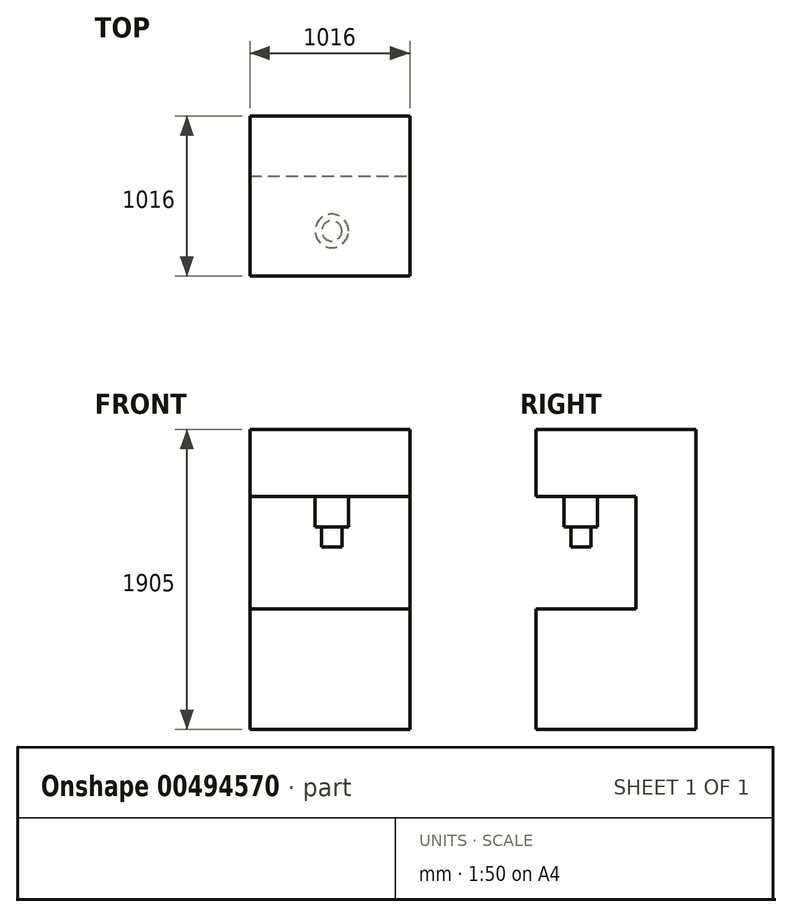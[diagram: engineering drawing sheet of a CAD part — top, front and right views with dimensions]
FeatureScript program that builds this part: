
annotation { "Feature Type Name" : "Feature", "Feature Type Description" : "" }
export const myFeature = defineFeature(function(context is Context, id is Id, definition is map)
    precondition{}
    {
        {
            var Q0;
            Q0=qCreatedBy(makeId("Front.planeOp"),FACE);
            var sketch = newSketch(context, id + "F0", { "sketchPlane" : qUnion([Q0])});
            skLineSegment(sketch, "E0.bottom", {"start": v(0, 0) * mm, "end": v(-1016, 0) * mm});
            skLineSegment(sketch, "E0.top", {"start": v(0, 1905) * mm, "end": v(-1016, 1905) * mm});
            skLineSegment(sketch, "E0.left", {"start": v(0, 0) * mm, "end": v(0, 1905) * mm});
            skLineSegment(sketch, "E0.right", {"start": v(-1016, 0) * mm, "end": v(-1016, 1905) * mm});
            skSolve(sketch);
        }
        {
            var Q0;
            Q0=makeQuery(id+"F0.imprint","IMPRINT",FACE,{"disambiguationData":[TD([[makeQuery(id+"F0.imprint","IMPRINT",EDGE,{"derivedFrom":sQuery(id+"F0.wireOp",EDGE,"E0.bottom")}),-1.0]])]});
            extrude(context, id + "F1", {"entities" : qUnion([Q0]), "depth" : 1016 * mm});
        }
        {
            var Q0;
            Q0=makeQuery(id+"F1.opExtrude","CAP_FACE",FACE,{"disambiguationData":[OSD([sQuery(id+"F0.wireOp",EDGE,"E0.bottom"),sQuery(id+"F0.wireOp",EDGE,"E0.top"),sQuery(id+"F0.wireOp",EDGE,"E0.left"),sQuery(id+"F0.wireOp",EDGE,"E0.right")])],"isStart":false});
            var sketch = newSketch(context, id + "F2", { "sketchPlane" : qUnion([Q0])});
            skLineSegment(sketch, "E1.bottom", {"start": v(-1016, 1478.3) * mm, "end": v(0, 1478.3) * mm});
            skLineSegment(sketch, "E1.top", {"start": v(-1016, 765.22) * mm, "end": v(0, 765.22) * mm});
            skLineSegment(sketch, "E1.left", {"start": v(-1016, 1478.3) * mm, "end": v(-1016, 765.22) * mm});
            skLineSegment(sketch, "E1.right", {"start": v(0, 1478.3) * mm, "end": v(0, 765.22) * mm});
            skSolve(sketch);
        }
        {
            var Q0;
            Q0=makeQuery(id+"F2.imprint","IMPRINT",FACE,{"disambiguationData":[TD([[makeQuery(id+"F2.imprint","IMPRINT",EDGE,{"derivedFrom":sQuery(id+"F2.wireOp",EDGE,"E1.bottom")}),-1.0]])]});
            extrude(context, id + "F3", {"entities" : qUnion([Q0]), "operationType" : NewBodyOperationType.REMOVE, "oppositeDirection" : true, "depth" : 635 * mm});
        }
        {
            var Q0;
            Q0=makeQuery(id+"F3.boolean.opBoolean","COPY",FACE,{"derivedFrom":makeQuery(id+"F3.opExtrude","SWEPT_FACE",FACE,{"disambiguationData":[OSD([sQuery(id+"F2.wireOp",EDGE,"E1.bottom")])]})});
            var sketch = newSketch(context, id + "F4", { "sketchPlane" : qUnion([Q0])});
            skCircle(sketch, "E2", {"center": v(-495.64, 729.41) * mm, "radius": 106.51 * mm});
            skSolve(sketch);
        }
        {
            var Q0;
            Q0 = qSketchRegion(id + "F4", true);
            extrude(context, id + "F5", {"entities" : qUnion([Q0]), "operationType" : NewBodyOperationType.ADD, "depth" : 193.04 * mm});
        }
        {
            var Q0;
            Q0=makeQuery(id+"F5.opExtrude","CAP_FACE",FACE,{"disambiguationData":[OSD([sQuery(id+"F4.wireOp",EDGE,"E2")])],"isStart":false});
            var sketch = newSketch(context, id + "F6", { "sketchPlane" : qUnion([Q0])});
            skCircle(sketch, "E3", {"center": v(-495.64, 729.41) * mm, "radius": 64.6 * mm});
            skSolve(sketch);
        }
        {
            var Q0;
            Q0=makeQuery(id+"F6.imprint","IMPRINT",FACE,{"disambiguationData":[TD([[makeQuery(id+"F6.imprint","IMPRINT",EDGE,{"derivedFrom":sQuery(id+"F6.wireOp",EDGE,"E3")}),1.0]])]});
            extrude(context, id + "F7", {"entities" : qUnion([Q0]), "operationType" : NewBodyOperationType.ADD, "depth" : 127 * mm});
        }
        {
            var Q0;
            Q0=makeQuery(id+"F7.opExtrude","CAP_FACE",FACE,{"disambiguationData":[OSD([sQuery(id+"F6.wireOp",EDGE,"E3")])],"isStart":false});
            var sketch = newSketch(context, id + "F8", { "sketchPlane" : qUnion([Q0])});
            skCircle(sketch, "E4", {"center": v(-495.64, 729.41) * mm, "radius": 29.88 * mm});
            skSolve(sketch);
        }
        {
            var Q0;
            Q0=sQuery(id+"F8.wireOp",EDGE,"E4");
            extrude(context, id + "F9", {"bodyType" : ToolBodyType.SURFACE, "surfaceEntities" : qUnion([Q0]), "depth" : 127 * mm});
        }
    });
